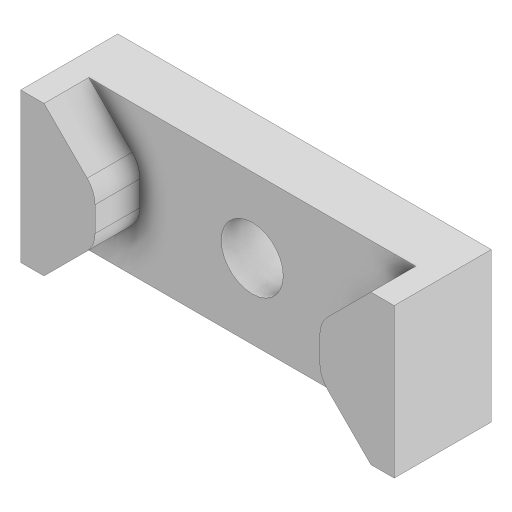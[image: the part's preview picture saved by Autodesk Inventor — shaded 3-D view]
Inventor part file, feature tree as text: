
AUTODESK INVENTOR PART (.ipt)
format: ipt  version: 2023 (Build 270158000, 158)  size: 150,528 bytes
history: native  units: mm
features: extrude x2, sketch x2, projected_geometry x1
ambient origin geometry x8: Origin, YZ Plane, XZ Plane, XY Plane, X Axis, Y Axis, Z Axis, Center Point
bodies: Solid1 (feature_tree)
feature tree (5):
  extrude  "Extrusion1"  Depth=25.0mm
  extrude  "Extrusion2"  Depth=3.5mm TaperAngle=0.0deg
  sketch  "Sketch1"  dims[d0=4.15mm d1=25.0mm]
  sketch  "Sketch3"  dims[d2=10.0mm d3=3.5mm d4=0.0mm d5=0.2mm d6=0.2mm d7=0.2mm d8=0.2mm d9=0.2mm d10=0.2mm d11=0.2mm d12=0.2mm d13=0.2mm d14=3.0mm d15=0.0mm d16=0.5mm d17=0.872665mm]
  projected_geometry  "Projected Loop1"
